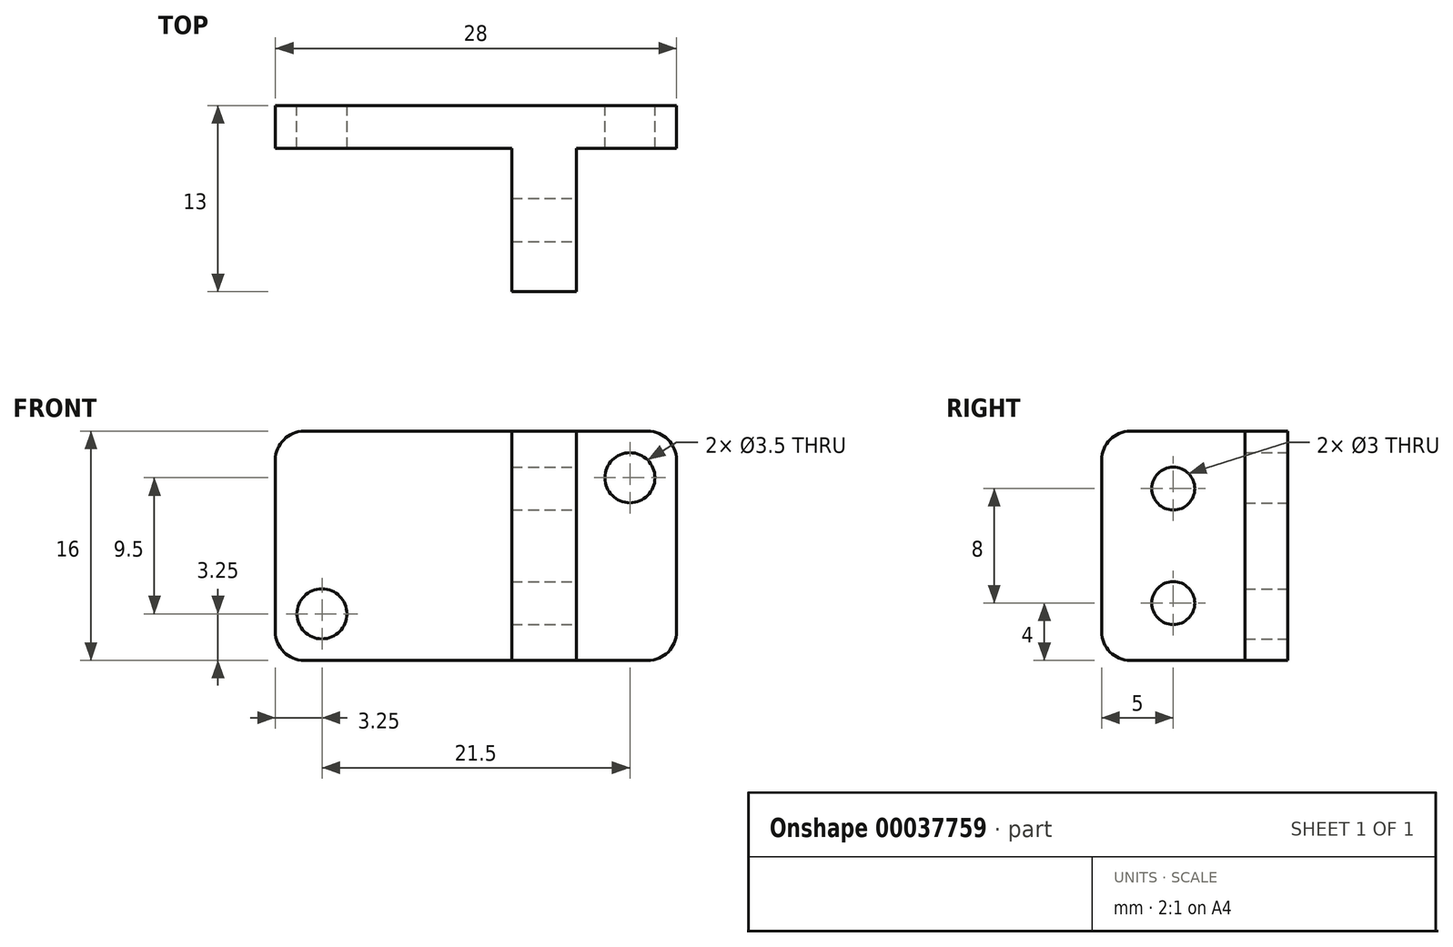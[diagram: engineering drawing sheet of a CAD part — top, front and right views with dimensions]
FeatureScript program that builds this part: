
annotation { "Feature Type Name" : "Feature", "Feature Type Description" : "" }
export const myFeature = defineFeature(function(context is Context, id is Id, definition is map)
    precondition{}
    {
        {
            var Q0;
            Q0=qCreatedBy(makeId("Front.planeOp"),FACE);
            var sketch = newSketch(context, id + "F0", { "sketchPlane" : qUnion([Q0])});
            skLineSegment(sketch, "E0.bottom", {"start": v(12, 8) * mm, "end": v(-12, 8) * mm});
            skLineSegment(sketch, "E0.top", {"start": v(12, -8) * mm, "end": v(-12, -8) * mm});
            skLineSegment(sketch, "E0.left", {"start": v(14, 6) * mm, "end": v(14, -6) * mm});
            skLineSegment(sketch, "E0.right", {"start": v(-14, 6) * mm, "end": v(-14, -6) * mm});
            skPoint(sketch, "E0.middle", {"position": v(0, 0) * mm});
            skPoint(sketch, "E1.visualSharp", {"position": v(14, 8) * mm});
            skArc(sketch, "E1.filletArc", {"start": v(14, 6) * mm, "mid": v(13.41, 7.41) * mm, "end": v(12, 8) * mm});
            skPoint(sketch, "E2.visualSharp", {"position": v(-14, 8) * mm});
            skArc(sketch, "E2.filletArc", {"start": v(-12, 8) * mm, "mid": v(-13.41, 7.41) * mm, "end": v(-14, 6) * mm});
            skPoint(sketch, "E3.visualSharp", {"position": v(-14, -8) * mm});
            skArc(sketch, "E3.filletArc", {"start": v(-14, -6) * mm, "mid": v(-13.41, -7.41) * mm, "end": v(-12, -8) * mm});
            skPoint(sketch, "E4.visualSharp", {"position": v(14, -8) * mm});
            skArc(sketch, "E4.filletArc", {"start": v(12, -8) * mm, "mid": v(13.41, -7.41) * mm, "end": v(14, -6) * mm});
            skLineSegment(sketch, "E5", {"start": v(0, 13.24) * mm, "end": v(0, -13.26) * mm, "construction": true});
            skLineSegment(sketch, "E6", {"start": v(18.73, 0) * mm, "end": v(-17.21, 0) * mm, "construction": true});
            skCircle(sketch, "E7.MirrorC", {"center": v(-10.75, -4.75) * mm, "radius": 1.75 * mm});
            skCircle(sketch, "E8.MirrorC", {"center": v(10.75, 4.75) * mm, "radius": 1.75 * mm});
            skSolve(sketch);
        }
        {
            var Q0;
            Q0 = qSketchRegion(id + "F0", true);
            extrude(context, id + "F1", {"entities" : qUnion([Q0]), "depth" : 3 * mm, "symmetric" : true});
        }
        {
            var Q0;
            Q0=qCreatedBy(makeId("Right.planeOp"),FACE);
            cPlane(context, id + "F2", {"entities" : qUnion([Q0]), "cplaneType" : CPlaneType.OFFSET, "offset" : 4 * mm, "width" : 150 * mm, "height" : 150 * mm});
        }
        {
            var Q0;
            Q0=qCreatedBy(id+"F2.planeOp",FACE);
            var sketch = newSketch(context, id + "F3", { "sketchPlane" : qUnion([Q0])});
            skLineSegment(sketch, "E9.bottom", {"start": v(-1.5, -8) * mm, "end": v(-9.5, -8) * mm});
            skLineSegment(sketch, "E9.top", {"start": v(-1.5, 8) * mm, "end": v(-9.5, 8) * mm});
            skLineSegment(sketch, "E9.left", {"start": v(-1.5, -8) * mm, "end": v(-1.5, 8) * mm});
            skLineSegment(sketch, "E9.right", {"start": v(-11.5, -6) * mm, "end": v(-11.5, 6) * mm});
            skPoint(sketch, "E10.visualSharp", {"position": v(-11.5, 8) * mm});
            skArc(sketch, "E10.filletArc", {"start": v(-9.5, 8) * mm, "mid": v(-10.91, 7.41) * mm, "end": v(-11.5, 6) * mm});
            skPoint(sketch, "E11.visualSharp", {"position": v(-11.5, -8) * mm});
            skArc(sketch, "E11.filletArc", {"start": v(-11.5, -6) * mm, "mid": v(-10.91, -7.41) * mm, "end": v(-9.5, -8) * mm});
            skSolve(sketch);
        }
        {
            var Q0;
            Q0 = qSketchRegion(id + "F3", true);
            extrude(context, id + "F4", {"entities" : qUnion([Q0]), "operationType" : NewBodyOperationType.ADD, "depth" : 3 * mm});
        }
        {
            var Q0;
            Q0 = qSketchRegion(id + "F3", true);
            extrude(context, id + "F5", {"entities" : qUnion([Q0]), "operationType" : NewBodyOperationType.ADD, "depth" : 3 * mm, "symmetric" : true});
        }
        {
            var Q0;
            Q0=makeQuery(id+"F4.opExtrude","CAP_FACE",FACE,{"disambiguationData":[OSD([sQuery(id+"F3.wireOp",EDGE,"E9.bottom"),sQuery(id+"F3.wireOp",EDGE,"E9.top"),sQuery(id+"F3.wireOp",EDGE,"E9.left"),sQuery(id+"F3.wireOp",EDGE,"E9.right"),sQuery(id+"F3.wireOp",EDGE,"E10.filletArc"),sQuery(id+"F3.wireOp",EDGE,"E11.filletArc")])],"isStart":false});
            var sketch = newSketch(context, id + "F6", { "sketchPlane" : qUnion([Q0])});
            skLineSegment(sketch, "E12", {"start": v(-6.5, 12.94) * mm, "end": v(-6.5, -13.87) * mm, "construction": true});
            skCircle(sketch, "E13", {"center": v(-6.5, 4) * mm, "radius": 1.5 * mm});
            skLineSegment(sketch, "E14", {"start": v(-9.2, 0) * mm, "end": v(-3.98, 0) * mm, "construction": true});
            skCircle(sketch, "E15.MirrorC", {"center": v(-6.5, -4) * mm, "radius": 1.5 * mm});
            skSolve(sketch);
        }
        {
            var Q0;
            Q0 = qSketchRegion(id + "F6", true);
            extrude(context, id + "F7", {"entities" : qUnion([Q0]), "operationType" : NewBodyOperationType.REMOVE, "endBound" : BoundingType.THROUGH_ALL, "oppositeDirection" : true, "depth" : 25 * mm});
        }
    });
